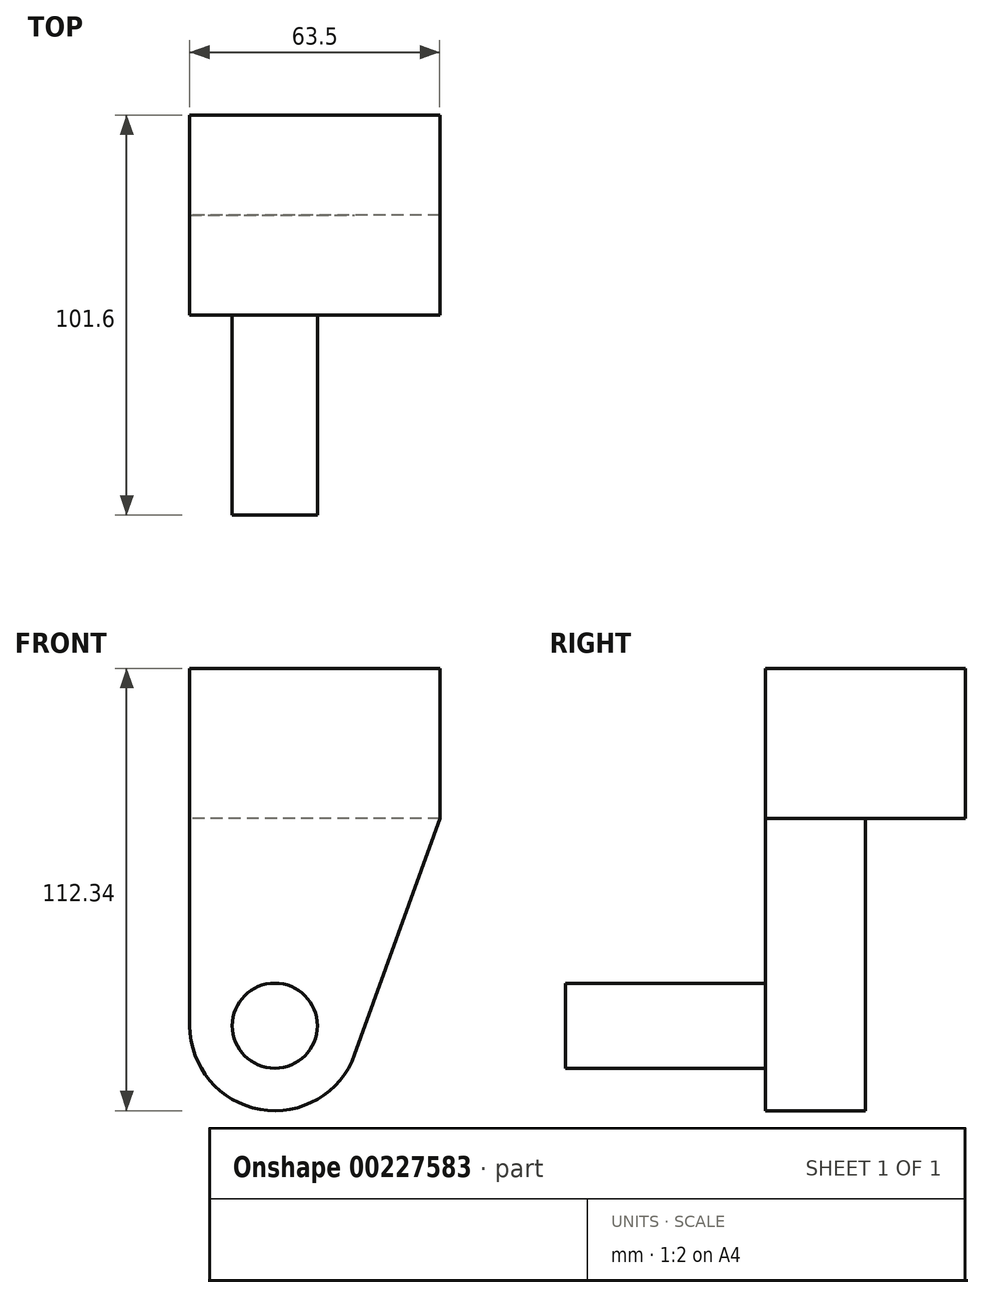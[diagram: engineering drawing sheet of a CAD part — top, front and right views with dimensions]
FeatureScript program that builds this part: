
annotation { "Feature Type Name" : "Feature", "Feature Type Description" : "" }
export const myFeature = defineFeature(function(context is Context, id is Id, definition is map)
    precondition{}
    {
        {
            var Q0;
            Q0=qCreatedBy(makeId("Front.planeOp"),FACE);
            var sketch = newSketch(context, id + "F0", { "sketchPlane" : qUnion([Q0])});
            skLineSegment(sketch, "E0", {"start": v(-33.76, 52.3) * mm, "end": v(29.74, 52.3) * mm});
            skLineSegment(sketch, "E1", {"start": v(29.74, 52.3) * mm, "end": v(29.74, 14.2) * mm});
            skLineSegment(sketch, "E2", {"start": v(29.74, 14.2) * mm, "end": v(-33.76, 14.2) * mm});
            skLineSegment(sketch, "E3", {"start": v(-33.76, 14.2) * mm, "end": v(-33.76, 52.3) * mm});
            skCircle(sketch, "E4", {"center": v(-12.17, -38.45) * mm, "radius": 21.59 * mm});
            skLineSegment(sketch, "E5", {"start": v(-33.76, 14.2) * mm, "end": v(-33.76, -38.45) * mm});
            skLineSegment(sketch, "E6", {"start": v(29.74, 14.2) * mm, "end": v(8.14, -45.77) * mm});
            skSolve(sketch);
        }
        {
            var Q0;
            Q0 = qSketchRegion(id + "F0", true);
            extrude(context, id + "F1", {"entities" : qUnion([Q0]), "depth" : 25.4 * mm});
        }
        {
            var Q0;
            Q0=qCreatedBy(makeId("Front.planeOp"),FACE);
            var sketch = newSketch(context, id + "F2", { "sketchPlane" : qUnion([Q0])});
            skCircle(sketch, "E7", {"center": v(-12.17, -38.45) * mm, "radius": 10.8 * mm});
            skSolve(sketch);
        }
        {
            var Q0;
            Q0=makeQuery(id+"F2.imprint","IMPRINT",FACE,{"disambiguationData":[TD([[makeQuery(id+"F2.imprint","IMPRINT",EDGE,{"derivedFrom":sQuery(id+"F2.wireOp",EDGE,"E7")}),1.0]])]});
            extrude(context, id + "F3", {"entities" : qUnion([Q0]), "operationType" : NewBodyOperationType.ADD, "depth" : 76.2 * mm});
        }
        {
            var Q0;
            Q0=makeQuery(id+"F1.opExtrude","CAP_FACE",FACE,{"disambiguationData":[OSD([sQuery(id+"F0.wireOp",EDGE,"E0"),sQuery(id+"F0.wireOp",EDGE,"E1"),sQuery(id+"F0.wireOp",EDGE,"E3"),sQuery(id+"F0.wireOp",EDGE,"E4"),sQuery(id+"F0.wireOp",EDGE,"E5"),sQuery(id+"F0.wireOp",EDGE,"E6")])],"isStart":true});
            var sketch = newSketch(context, id + "F4", { "sketchPlane" : qUnion([Q0])});
            skLineSegment(sketch, "E8", {"start": v(-29.74, 14.2) * mm, "end": v(33.76, 14.2) * mm});
            skSolve(sketch);
        }
        {
            var Q0;
            {var subQ0=sQuery(id+"F4.wireOp",EDGE,"E8");Q0=makeQuery(id+"F4.imprint","IMPRINT",FACE,{"disambiguationData":[TD([[makeQuery(id+"F4.imprint","IMPRINT",EDGE,{"derivedFrom":subQ0}),1.0]])]});}
            extrude(context, id + "F5", {"entities" : qUnion([Q0]), "operationType" : NewBodyOperationType.ADD, "depth" : 25.4 * mm});
        }
    });
